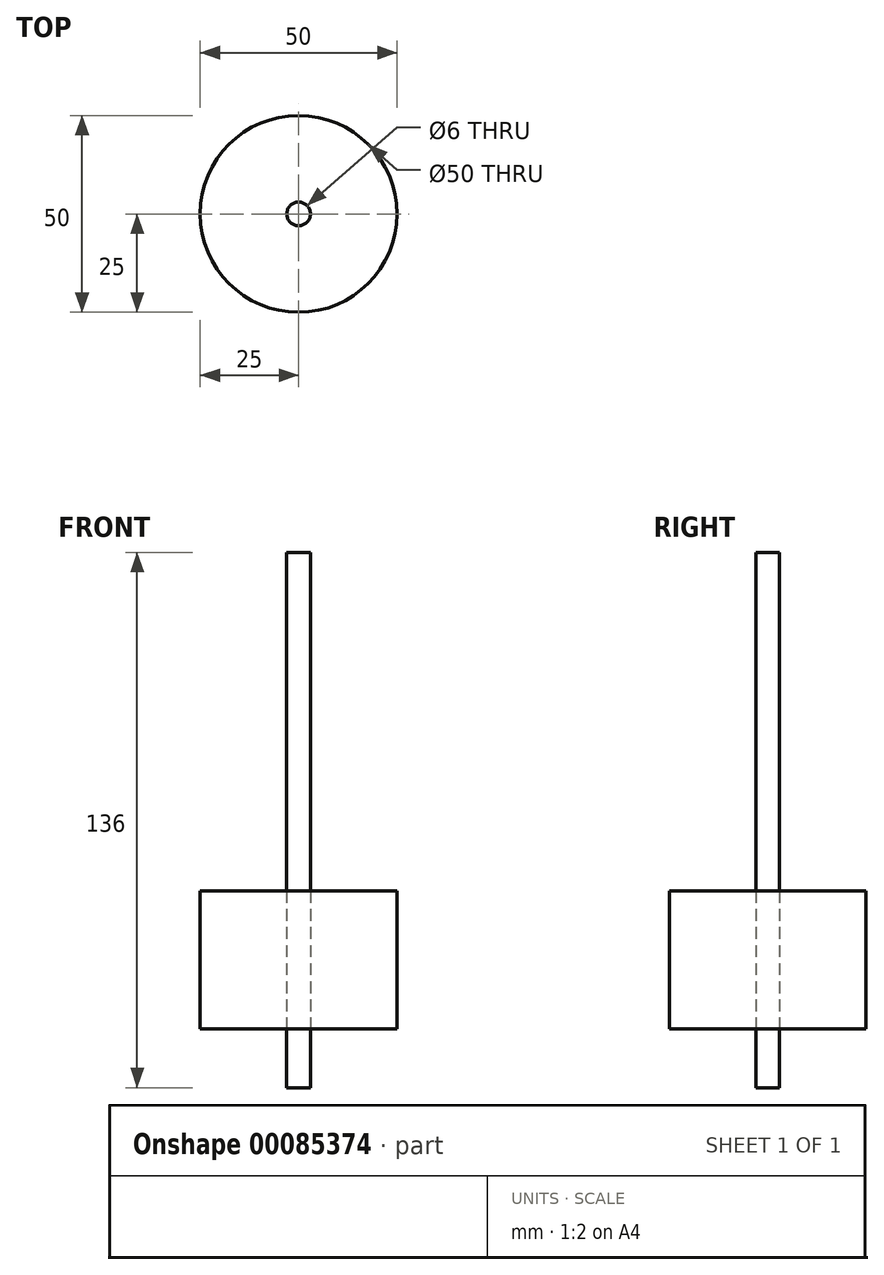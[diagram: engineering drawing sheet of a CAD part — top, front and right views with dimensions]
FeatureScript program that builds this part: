
annotation { "Feature Type Name" : "Feature", "Feature Type Description" : "" }
export const myFeature = defineFeature(function(context is Context, id is Id, definition is map)
    precondition{}
    {
        {
            var Q0;
            Q0=qCreatedBy(makeId("Top.planeOp"),FACE);
            var sketch = newSketch(context, id + "F0", { "sketchPlane" : qUnion([Q0])});
            skCircle(sketch, "E0", {"center": v(0, 0) * mm, "radius": 3 * mm});
            skCircle(sketch, "E1", {"center": v(0, 0) * mm, "radius": 9.5 * mm});
            skCircle(sketch, "E2", {"center": v(0, 0) * mm, "radius": 17.5 * mm, "construction": true});
            skCircle(sketch, "E3", {"center": v(0, 0) * mm, "radius": 25 * mm});
            skCircle(sketch, "E4", {"center": v(-17.5, 0) * mm, "radius": 2 * mm});
            skCircle(sketch, "E5", {"center": v(17.5, 0) * mm, "radius": 2 * mm});
            skSolve(sketch);
        }
        {
            var Q0;
            Q0=sQuery(id+"F0.wireOp",EDGE,"E0");
            extrude(context, id + "F1", {"bodyType" : ToolBodyType.SURFACE, "surfaceEntities" : qUnion([Q0]), "depth" : 86 * mm});
        }
        {
            var Q0;
            Q0=sQuery(id+"F0.wireOp",EDGE,"E0");
            extrude(context, id + "F2", {"bodyType" : ToolBodyType.SURFACE, "surfaceEntities" : qUnion([Q0]), "oppositeDirection" : true, "depth" : 50 * mm});
        }
        {
            var Q0;
            Q0=sQuery(id+"F0.wireOp",EDGE,"E3");
            extrude(context, id + "F3", {"bodyType" : ToolBodyType.SURFACE, "surfaceEntities" : qUnion([Q0]), "oppositeDirection" : true, "depth" : 35 * mm});
        }
    });
